# Revit family: Faucet-Valves_and_Controls-KOHLER-MODULO-K-98699T_1
name_source: partatom
category: Plumbing Fixtures
revit_build: Autodesk Revit 2017 (Build: 20160225_1515(x64)
units: mm (PartAtom-declared; Revit-internal decimal feet)

## family parameters
Cut with Voids When Loaded = No
Host = Face
OmniClass Number = 23.27.31.00
OmniClass Title = Valves
Part Type = Normal
Room Calculation Point = No
Round Connector Dimension = Use Diameter
Shared = No

## types (1)
- NA-Brass
    ADA Compliant = No
    Assembly Code = D2020
    CW Connection = Yes
    Cold Water Inlet = Cold Water Inlet
    Date Modified = 06/2/2020
    Default Elevation = 36"
    Description = Smart Universal Mounting Box
    Drain Included = No
    Finish = Kohler-Plastic-Blue
    Flow Rate = 0 GPM
    HW Connection = Yes
    Height = 6 1/8"
    Hot Water Inlet = Hot Water Inlet
    Length = 5 1/2"
    Manufacturer = KOHLER Co.
    MasterFormat 1995 = 154300
    MasterFormat 2004 = 22.41.39
    Material = Plastic
    Model = K-98699T-NA
    Pressure = 0.00 psi
    Product Documentation Link = http://files.kohler.com.cn
    Product Name = MODULO
    Product Page URL = http://www.kohler.com.cn
    Tempered Water Outlet 1 = Tempered Water Outlet 1
    Tempered Water Outlet 2 = Tempered Water Outlet 2
    URL = http://www.kohler.com.cn
    Vent Connection = No
    Waste Connection = No
    WaterSense Certified = No
    Width = 7 7/16"

## geometry (parser evidence)
native form markers: Sweep x5
no freeform markers — native parametric forms only
